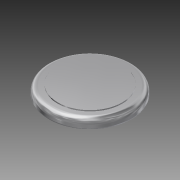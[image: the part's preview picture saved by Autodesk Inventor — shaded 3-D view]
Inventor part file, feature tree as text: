
AUTODESK INVENTOR PART (.ipt)
format: ipt  version: 2014 (Build 180170000, 170)  size: 116,224 bytes
history: native  units: in
note: dims shown in document units (in); Inventor stores cm internally (conversion verified against a paired STEP export)
features: revolve x1, sketch x1
ambient origin geometry x8: Origin, YZ Plane, XZ Plane, XY Plane, X Axis, Y Axis, Z Axis, Center Point
bodies: Solid1 (feature_tree)
feature tree (2):
  revolve  "Revolution1"  [1 undecoded]
  sketch  "Sketch1"  dims[d1=0.0787in d2=0.015in d3=0.04in d4=90.0deg]
note: 1 required parameter value undecoded (feature->parameter linkage not recoverable at this tier; creation-order binding heuristic only, values carry confidence <= 0.55)
